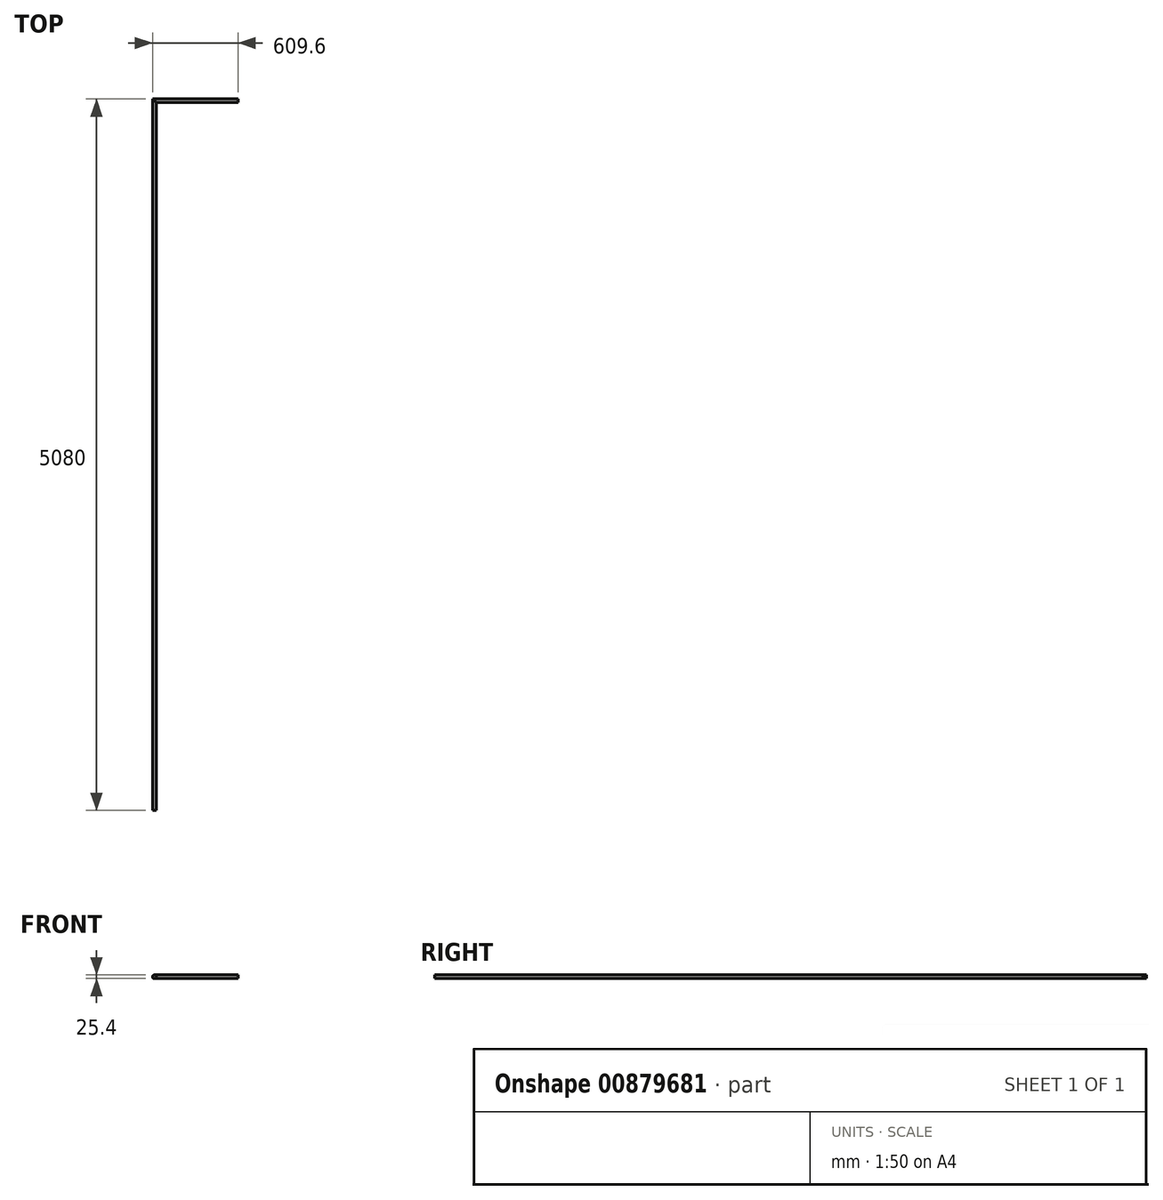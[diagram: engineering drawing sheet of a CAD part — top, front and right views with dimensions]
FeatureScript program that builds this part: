
annotation { "Feature Type Name" : "Feature", "Feature Type Description" : "" }
export const myFeature = defineFeature(function(context is Context, id is Id, definition is map)
    precondition{}
    {
        {
            var Q0;
            Q0=qCreatedBy(makeId("Top.planeOp"),FACE);
            var sketch = newSketch(context, id + "F0", { "sketchPlane" : qUnion([Q0])});
            skLineSegment(sketch, "E0", {"start": v(0, -42.37) * mm, "end": v(0, 5024.93) * mm});
            skLineSegment(sketch, "E1", {"start": v(0, 5024.93) * mm, "end": v(596.9, 5024.93) * mm});
            skLineSegment(sketch, "E2", {"start": v(596.9, 5024.93) * mm, "end": v(596.9, 5037.63) * mm});
            skLineSegment(sketch, "E3", {"start": v(596.9, 5037.63) * mm, "end": v(-12.7, 5037.63) * mm});
            skLineSegment(sketch, "E4", {"start": v(-12.7, 5037.63) * mm, "end": v(-12.7, -42.37) * mm});
            skLineSegment(sketch, "E5", {"start": v(-12.7, -42.37) * mm, "end": v(0, -42.37) * mm});
            skLineSegment(sketch, "E6", {"start": v(0, 5024.93) * mm, "end": v(0, 5037.63) * mm});
            skSolve(sketch);
        }
        {
            var Q0;
            Q0=makeQuery(id+"F0.imprint","IMPRINT",FACE,{"disambiguationData":[TD([[makeQuery(id+"F0.imprint","IMPRINT",EDGE,{"derivedFrom":sQuery(id+"F0.wireOp",EDGE,"E0")}),1.0]])]});
            var Q1;
            Q1=sQuery(id+"F0.wireOp",EDGE,"E0");
            revolve(context, id + "F1", {"surfaceOperationType" : NewSurfaceOperationType.NEW, "entities" : qUnion([Q0]), "axis" : qUnion([Q1]), "revolveType" : RevolveType.FULL});
        }
        {
            var Q0;
            Q0=makeQuery(id+"F0.imprint","IMPRINT",FACE,{"disambiguationData":[TD([[makeQuery(id+"F0.imprint","IMPRINT",EDGE,{"derivedFrom":sQuery(id+"F0.wireOp",EDGE,"E1")}),1.0]])]});
            var Q1;
            Q1=sQuery(id+"F0.wireOp",EDGE,"E1");
            revolve(context, id + "F2", {"operationType" : NewBodyOperationType.ADD, "surfaceOperationType" : NewSurfaceOperationType.NEW, "entities" : qUnion([Q0]), "axis" : qUnion([Q1]), "revolveType" : RevolveType.FULL});
        }
    });
